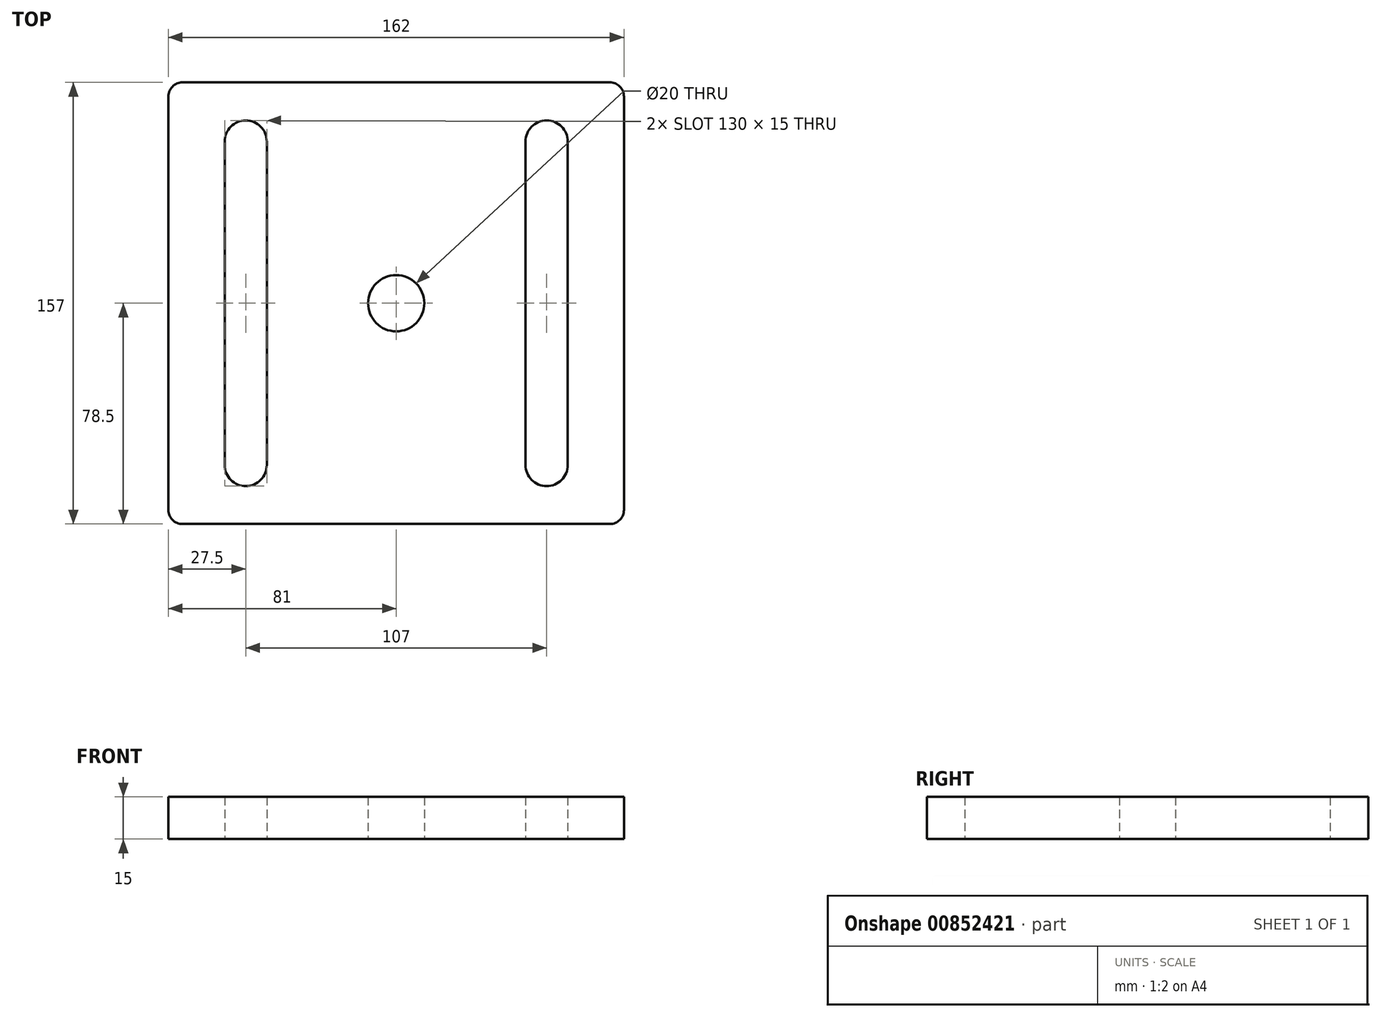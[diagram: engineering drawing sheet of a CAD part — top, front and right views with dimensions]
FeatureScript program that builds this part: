
annotation { "Feature Type Name" : "Feature", "Feature Type Description" : "" }
export const myFeature = defineFeature(function(context is Context, id is Id, definition is map)
    precondition{}
    {
        {
            var Q0;
            Q0=qCreatedBy(makeId("Top.planeOp"),FACE);
            var sketch = newSketch(context, id + "F0", { "sketchPlane" : qUnion([Q0])});
            skLineSegment(sketch, "E0.bottom", {"start": v(-76, 78.5) * mm, "end": v(76, 78.5) * mm});
            skLineSegment(sketch, "E0.top", {"start": v(-76, -78.5) * mm, "end": v(76, -78.5) * mm});
            skLineSegment(sketch, "E0.left", {"start": v(-81, 73.5) * mm, "end": v(-81, -73.5) * mm});
            skLineSegment(sketch, "E0.right", {"start": v(81, 73.5) * mm, "end": v(81, -73.5) * mm});
            skPoint(sketch, "E0.middle", {"position": v(0, 0) * mm});
            skPoint(sketch, "E1.visualSharp", {"position": v(-81, 78.5) * mm});
            skArc(sketch, "E1.filletArc", {"start": v(-76, 78.5) * mm, "mid": v(-79.54, 77.04) * mm, "end": v(-81, 73.5) * mm});
            skPoint(sketch, "E2.visualSharp", {"position": v(81, 78.5) * mm});
            skArc(sketch, "E2.filletArc", {"start": v(81, 73.5) * mm, "mid": v(79.54, 77.04) * mm, "end": v(76, 78.5) * mm});
            skPoint(sketch, "E3.visualSharp", {"position": v(81, -78.5) * mm});
            skArc(sketch, "E3.filletArc", {"start": v(76, -78.5) * mm, "mid": v(79.54, -77.04) * mm, "end": v(81, -73.5) * mm});
            skPoint(sketch, "E4.visualSharp", {"position": v(-81, -78.5) * mm});
            skArc(sketch, "E4.filletArc", {"start": v(-81, -73.5) * mm, "mid": v(-79.54, -77.04) * mm, "end": v(-76, -78.5) * mm});
            skCircle(sketch, "E5", {"center": v(0, 0) * mm, "radius": 10 * mm});
            skLineSegment(sketch, "E6", {"start": v(-53.5, 57.5) * mm, "end": v(-53.5, 0) * mm, "construction": true});
            skArc(sketch, "E7", {"start": v(-46, 57.5) * mm, "mid": v(-53.5, 65) * mm, "end": v(-61, 57.5) * mm});
            skLineSegment(sketch, "E8", {"start": v(-61, 57.5) * mm, "end": v(-61, 0) * mm});
            skLineSegment(sketch, "E9", {"start": v(-46, 57.5) * mm, "end": v(-46, 0) * mm});
            skLineSegment(sketch, "E10.MirrorCS", {"start": v(-46, -57.5) * mm, "end": v(-46, 0) * mm});
            skArc(sketch, "E11.MirrorCS", {"start": v(-46, -57.5) * mm, "mid": v(-53.5, -65) * mm, "end": v(-61, -57.5) * mm});
            skLineSegment(sketch, "E12.MirrorCS", {"start": v(-61, -57.5) * mm, "end": v(-61, 0) * mm});
            skLineSegment(sketch, "E13.MirrorCS", {"start": v(46, 57.5) * mm, "end": v(46, 0) * mm});
            skArc(sketch, "E14.MirrorCS", {"start": v(46, 57.5) * mm, "mid": v(53.5, 65) * mm, "end": v(61, 57.5) * mm});
            skLineSegment(sketch, "E15.MirrorCS", {"start": v(61, 57.5) * mm, "end": v(61, 0) * mm});
            skLineSegment(sketch, "E16.MirrorCS", {"start": v(61, -57.5) * mm, "end": v(61, 0) * mm});
            skArc(sketch, "E17.MirrorCS", {"start": v(46, -57.5) * mm, "mid": v(53.5, -65) * mm, "end": v(61, -57.5) * mm});
            skLineSegment(sketch, "E18.MirrorCS", {"start": v(46, -57.5) * mm, "end": v(46, 0) * mm});
            skSolve(sketch);
        }
        {
            var Q0;
            Q0=makeQuery(id+"F0.imprint","IMPRINT",FACE,{"disambiguationData":[TD([[makeQuery(id+"F0.imprint","IMPRINT",EDGE,{"derivedFrom":sQuery(id+"F0.wireOp",EDGE,"E0.bottom")}),-1.0]])]});
            extrude(context, id + "F1", {"entities" : qUnion([Q0]), "depth" : 15 * mm, "offsetDistance" : 25 * mm});
        }
    });
